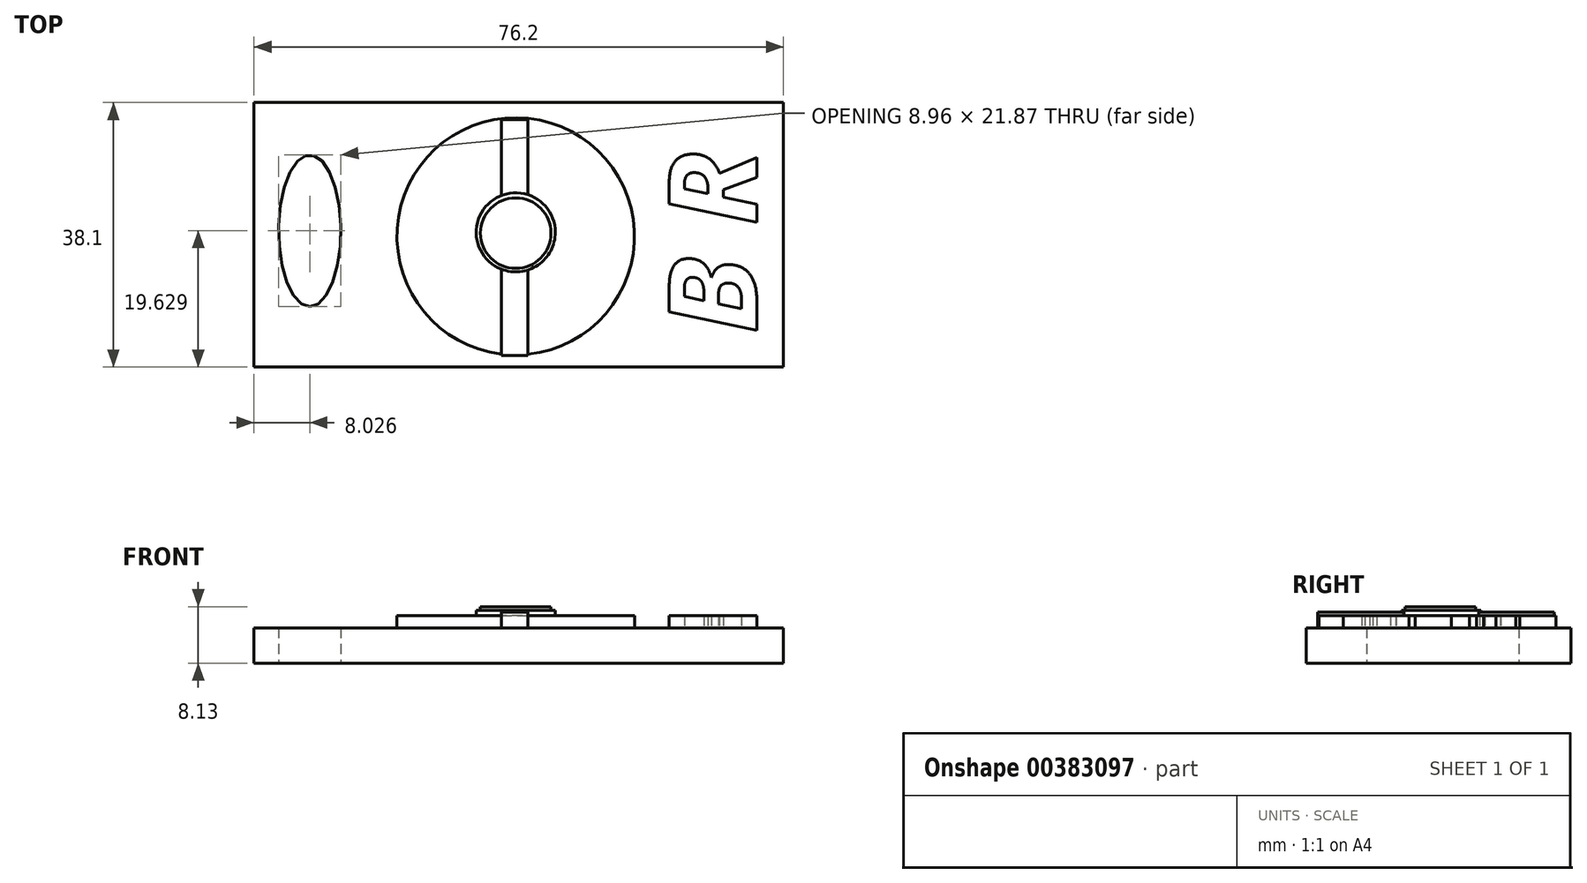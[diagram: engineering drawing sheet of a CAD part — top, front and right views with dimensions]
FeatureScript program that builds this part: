
annotation { "Feature Type Name" : "Feature", "Feature Type Description" : "" }
export const myFeature = defineFeature(function(context is Context, id is Id, definition is map)
    precondition{}
    {
        {
            var Q0;
            Q0=qCreatedBy(makeId("Top.planeOp"),FACE);
            var sketch = newSketch(context, id + "F0", { "sketchPlane" : qUnion([Q0])});
            skLineSegment(sketch, "E0.bottom", {"start": v(38.53, 22.5) * mm, "end": v(-37.67, 22.5) * mm});
            skLineSegment(sketch, "E0.top", {"start": v(38.53, -15.6) * mm, "end": v(-37.67, -15.6) * mm});
            skLineSegment(sketch, "E0.left", {"start": v(38.53, 22.5) * mm, "end": v(38.53, -15.6) * mm});
            skLineSegment(sketch, "E0.right", {"start": v(-37.67, 22.5) * mm, "end": v(-37.67, -15.6) * mm});
            skSolve(sketch);
        }
        {
            var Q0;
            Q0=makeQuery(id+"F0.imprint","IMPRINT",FACE,{"disambiguationData":[TD([[makeQuery(id+"F0.imprint","IMPRINT",EDGE,{"derivedFrom":sQuery(id+"F0.wireOp",EDGE,"E0.bottom")}),1.0]])]});
            extrude(context, id + "F1", {"entities" : qUnion([Q0]), "depth" : 5.08 * mm});
        }
        {
            var Q0;
            Q0=qCreatedBy(makeId("Top.planeOp"),FACE);
            var sketch = newSketch(context, id + "F2", { "sketchPlane" : qUnion([Q0])});
            skEllipse(sketch, "E1", {"center": v(-29.64, 4.03) * mm, "majorRadius": 10.93 * mm, "minorRadius": 4.48 * mm, "majorAxis": v(0, -1)});
            skSolve(sketch);
        }
        {
            var Q0;
            Q0 = qSketchRegion(id + "F2", true);
            extrude(context, id + "F3", {"entities" : qUnion([Q0]), "operationType" : NewBodyOperationType.REMOVE, "depth" : 25.4 * mm});
        }
        {
            var Q0;
            Q0=qCreatedBy(makeId("Top.planeOp"),FACE);
            var sketch = newSketch(context, id + "F4", { "sketchPlane" : qUnion([Q0])});
            skCircle(sketch, "E2", {"center": v(0, 3.23) * mm, "radius": 17.09 * mm});
            skSolve(sketch);
        }
        {
            var Q0;
            Q0 = qSketchRegion(id + "F4", true);
            extrude(context, id + "F5", {"entities" : qUnion([Q0]), "operationType" : NewBodyOperationType.ADD, "depth" : 6.86 * mm});
        }
        {
            var Q0;
            Q0=qCreatedBy(makeId("Top.planeOp"),FACE);
            var sketch = newSketch(context, id + "F6", { "sketchPlane" : qUnion([Q0])});
            skLineSegment(sketch, "E3.bottom", {"start": v(1.78, 20.05) * mm, "end": v(-2.1, 20.05) * mm});
            skLineSegment(sketch, "E3.top", {"start": v(1.78, -13.95) * mm, "end": v(-2.1, -13.95) * mm});
            skLineSegment(sketch, "E3.left", {"start": v(1.78, 20.05) * mm, "end": v(1.78, -13.95) * mm});
            skLineSegment(sketch, "E3.right", {"start": v(-2.1, 20.05) * mm, "end": v(-2.1, -13.95) * mm});
            skSolve(sketch);
        }
        {
            var Q0;
            Q0 = qSketchRegion(id + "F6", true);
            extrude(context, id + "F7", {"entities" : qUnion([Q0]), "operationType" : NewBodyOperationType.ADD, "depth" : 7.37 * mm});
        }
        {
            var Q0;
            Q0=qCreatedBy(makeId("Top.planeOp"),FACE);
            var sketch = newSketch(context, id + "F8", { "sketchPlane" : qUnion([Q0])});
            skCircle(sketch, "E4", {"center": v(0, 3.8) * mm, "radius": 5.7 * mm});
            skSolve(sketch);
        }
        {
            var Q0;
            Q0 = qSketchRegion(id + "F8", true);
            extrude(context, id + "F9", {"entities" : qUnion([Q0]), "operationType" : NewBodyOperationType.ADD, "depth" : 7.62 * mm});
        }
        {
            var Q0;
            Q0=qCreatedBy(makeId("Top.planeOp"),FACE);
            var sketch = newSketch(context, id + "F10", { "sketchPlane" : qUnion([Q0])});
            skCircle(sketch, "E5", {"center": v(0, 3.69) * mm, "radius": 5.08 * mm});
            skSolve(sketch);
        }
        {
            var Q0;
            Q0 = qSketchRegion(id + "F10", true);
            extrude(context, id + "F11", {"entities" : qUnion([Q0]), "operationType" : NewBodyOperationType.ADD, "depth" : 8.13 * mm});
        }
        {
            var Q0;
            Q0=qCreatedBy(makeId("Top.planeOp"),FACE);
            var sketch = newSketch(context, id + "F12", { "sketchPlane" : qUnion([Q0])});
            skText(sketch, "E6", { "text": "B R", "fontName": "OpenSans-BoldItalic.ttf"});
            const initialGuessF12  = {"E6": [0.03468, -0.01074, 0, 1, 0.0127]};
            skSetInitialGuess(sketch, initialGuessF12);
            skSolve(sketch);
        }
        {
            var Q0;
            Q0 = qSketchRegion(id + "F12", true);
            extrude(context, id + "F13", {"entities" : qUnion([Q0]), "operationType" : NewBodyOperationType.ADD, "depth" : 6.86 * mm});
        }
    });
